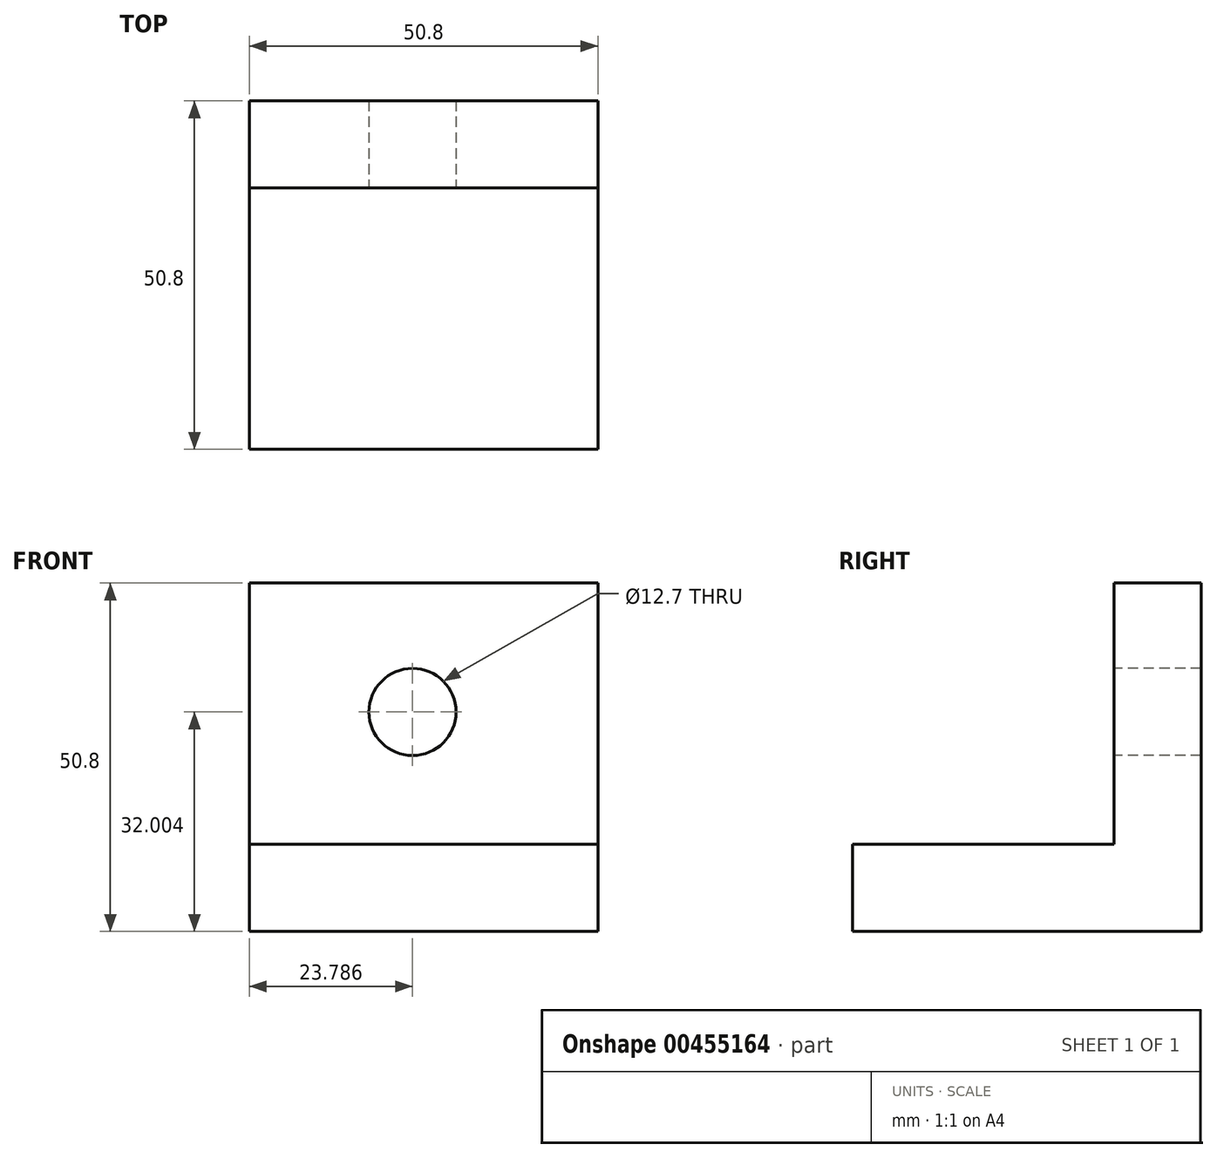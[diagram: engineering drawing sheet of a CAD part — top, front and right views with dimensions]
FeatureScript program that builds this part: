
annotation { "Feature Type Name" : "Feature", "Feature Type Description" : "" }
export const myFeature = defineFeature(function(context is Context, id is Id, definition is map)
    precondition{}
    {
        {
            var Q0;
            Q0=qCreatedBy(makeId("Top.planeOp"),FACE);
            var sketch = newSketch(context, id + "F0", { "sketchPlane" : qUnion([Q0])});
            skLineSegment(sketch, "E0.bottom", {"start": v(1.9, 18.57) * mm, "end": v(-48.9, 18.57) * mm});
            skLineSegment(sketch, "E0.top", {"start": v(1.9, -32.23) * mm, "end": v(-48.9, -32.23) * mm});
            skLineSegment(sketch, "E0.left", {"start": v(1.9, 18.57) * mm, "end": v(1.9, -32.23) * mm});
            skLineSegment(sketch, "E0.right", {"start": v(-48.9, 18.57) * mm, "end": v(-48.9, -32.23) * mm});
            skLineSegment(sketch, "E1", {"start": v(-48.9, 18.57) * mm, "end": v(-48.9, 5.87) * mm});
            skLineSegment(sketch, "E2", {"start": v(-48.9, 5.87) * mm, "end": v(1.9, 5.87) * mm});
            skSolve(sketch);
        }
        {
            var Q0;
            {var subQ0=sQuery(id+"F0.wireOp",EDGE,"E0.bottom");Q0=makeQuery(id+"F0.imprint","IMPRINT",FACE,{"disambiguationData":[TD([[makeQuery(id+"F0.imprint","IMPRINT",EDGE,{"derivedFrom":subQ0}),1.0]])]});}
            extrude(context, id + "F1", {"entities" : qUnion([Q0]), "depth" : 50.8 * mm});
        }
        {
            var Q0;
            Q0 = qSketchRegion(id + "F0", true);
            extrude(context, id + "F2", {"entities" : qUnion([Q0]), "operationType" : NewBodyOperationType.ADD, "depth" : 12.7 * mm});
        }
        {
            var Q0;
            Q0=qCreatedBy(makeId("Front.planeOp"),FACE);
            var sketch = newSketch(context, id + "F3", { "sketchPlane" : qUnion([Q0])});
            skCircle(sketch, "E3", {"center": v(-25.11, 32) * mm, "radius": 6.35 * mm});
            skSolve(sketch);
        }
        {
            var Q0;
            Q0=makeQuery(id+"F3.imprint","IMPRINT",FACE,{"disambiguationData":[TD([[makeQuery(id+"F3.imprint","IMPRINT",EDGE,{"derivedFrom":sQuery(id+"F3.wireOp",EDGE,"E3")}),1.0]])]});
            extrude(context, id + "F4", {"entities" : qUnion([Q0]), "operationType" : NewBodyOperationType.REMOVE, "endBound" : BoundingType.THROUGH_ALL, "oppositeDirection" : true, "depth" : 25.4 * mm});
        }
    });
